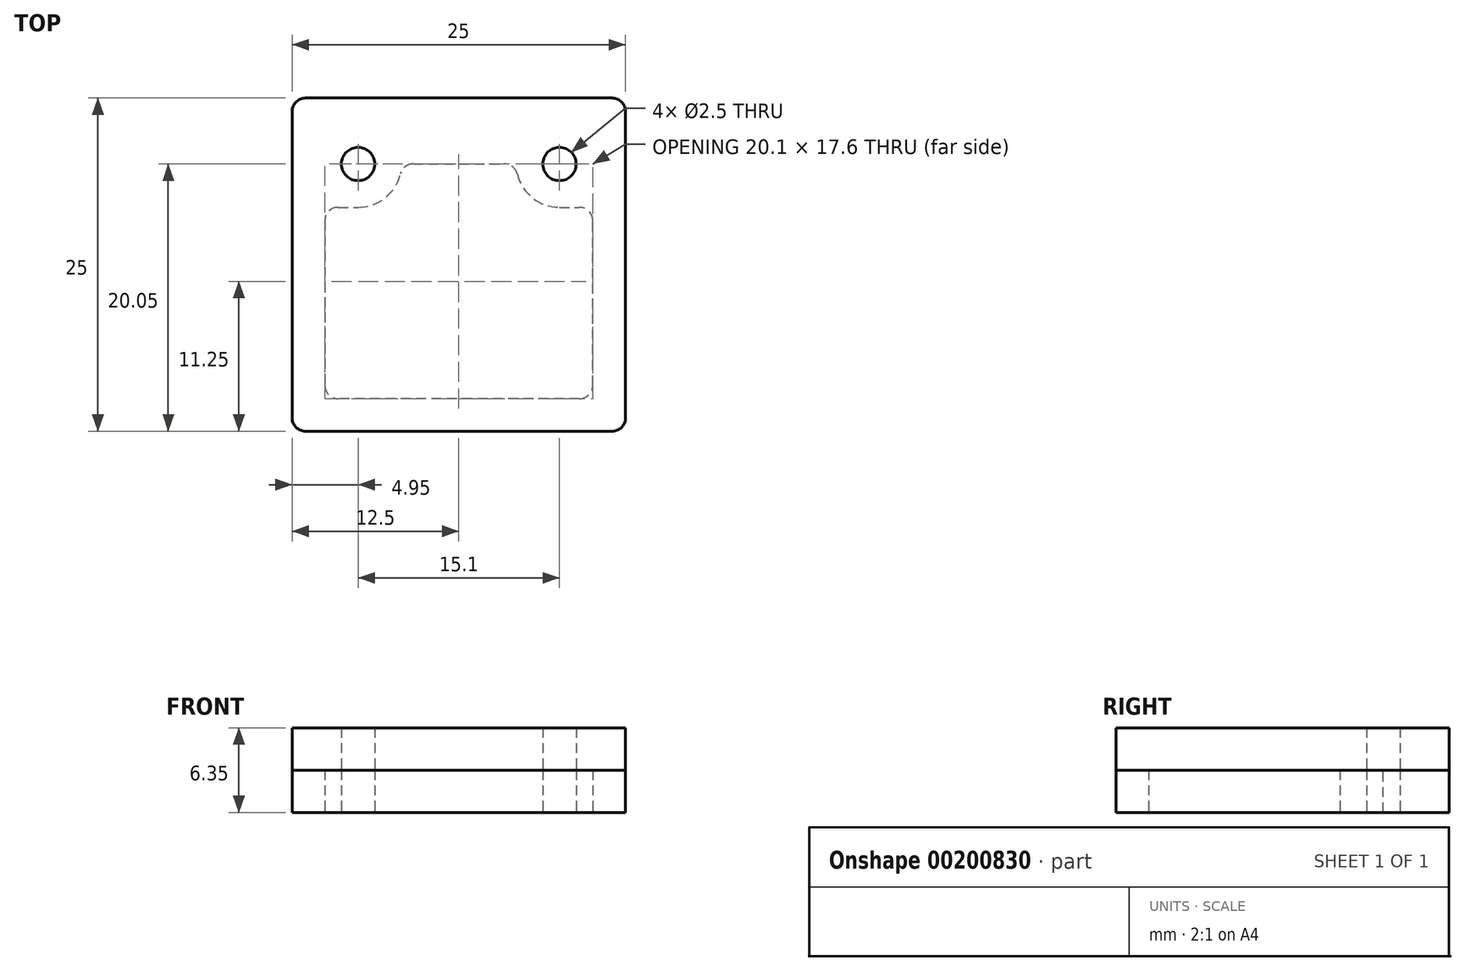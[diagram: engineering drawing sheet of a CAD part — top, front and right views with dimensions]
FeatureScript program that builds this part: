
annotation { "Feature Type Name" : "Feature", "Feature Type Description" : "" }
export const myFeature = defineFeature(function(context is Context, id is Id, definition is map)
    precondition{}
    {
        {
            var Q0;
            Q0=qCreatedBy(makeId("Top.planeOp"),FACE);
            var sketch = newSketch(context, id + "F0", { "sketchPlane" : qUnion([Q0])});
            skLineSegment(sketch, "E0.bottom", {"start": v(10.05, 10.05) * mm, "end": v(-10.05, 10.05) * mm});
            skLineSegment(sketch, "E0.top", {"start": v(10.05, -10.05) * mm, "end": v(-10.05, -10.05) * mm});
            skLineSegment(sketch, "E0.left", {"start": v(10.05, 10.05) * mm, "end": v(10.05, -10.05) * mm});
            skLineSegment(sketch, "E0.right", {"start": v(-10.05, 10.05) * mm, "end": v(-10.05, -10.05) * mm});
            skPoint(sketch, "E0.middle", {"position": v(0, 0) * mm});
            skCircle(sketch, "E1", {"center": v(-7.55, 7.55) * mm, "radius": 1.25 * mm});
            skLineSegment(sketch, "E2", {"start": v(0, 10.05) * mm, "end": v(0, -10.05) * mm, "construction": true});
            skCircle(sketch, "E3.MirrorC", {"center": v(7.55, 7.55) * mm, "radius": 1.25 * mm});
            skCircle(sketch, "E4.0", {"center": v(7.55, 7.55) * mm, "radius": 3.25 * mm});
            skCircle(sketch, "E5.0", {"center": v(-7.55, 7.55) * mm, "radius": 3.25 * mm});
            skLineSegment(sketch, "E6.bottom", {"start": v(12.5, 12.5) * mm, "end": v(-12.5, 12.5) * mm});
            skLineSegment(sketch, "E6.top", {"start": v(12.5, -12.5) * mm, "end": v(-12.5, -12.5) * mm});
            skLineSegment(sketch, "E6.left", {"start": v(12.5, 12.5) * mm, "end": v(12.5, -12.5) * mm});
            skLineSegment(sketch, "E6.right", {"start": v(-12.5, 12.5) * mm, "end": v(-12.5, -12.5) * mm});
            skSolve(sketch);
        }
        {
            var Q0;
            Q0=qCreatedBy(makeId("Top.planeOp"),FACE);
            var sketch = newSketch(context, id + "F1", { "sketchPlane" : qUnion([Q0])});
            skLineSegment(sketch, "E7.0", {"start": v(-12.5, 12.5) * mm, "end": v(-12.5, -12.5) * mm});
            skLineSegment(sketch, "E8.0", {"start": v(12.5, 12.5) * mm, "end": v(-12.5, 12.5) * mm});
            skLineSegment(sketch, "E9.0", {"start": v(12.5, 12.5) * mm, "end": v(12.5, -12.5) * mm});
            skLineSegment(sketch, "E10.0", {"start": v(12.5, -12.5) * mm, "end": v(-12.5, -12.5) * mm});
            skLineSegment(sketch, "E11.0", {"start": v(10.05, -10.05) * mm, "end": v(-10.05, -10.05) * mm});
            skArc(sketch, "E12.0", {"start": v(7.55, 4.3) * mm, "mid": v(5.25, 5.25) * mm, "end": v(4.3, 7.55) * mm});
            skArc(sketch, "E13.0.2", {"start": v(-4.3, 7.55) * mm, "mid": v(-5.25, 5.25) * mm, "end": v(-7.55, 4.3) * mm});
            skLineSegment(sketch, "E13.0.3", {"start": v(-10.05, 4.3) * mm, "end": v(-10.05, -10.05) * mm});
            skLineSegment(sketch, "E13.0.4", {"start": v(-10.05, -10.05) * mm, "end": v(10.05, -10.05) * mm});
            skLineSegment(sketch, "E13.0.5", {"start": v(10.05, -10.05) * mm, "end": v(10.05, 4.3) * mm});
            skLineSegment(sketch, "E14", {"start": v(-10.05, 4.3) * mm, "end": v(-7.55, 4.3) * mm});
            skLineSegment(sketch, "E15", {"start": v(7.55, 4.3) * mm, "end": v(10.05, 4.3) * mm});
            skLineSegment(sketch, "E16", {"start": v(-4.3, 7.55) * mm, "end": v(4.3, 7.55) * mm});
            skPoint(sketch, "E17.orphan", {"position": v(-5.47, 10.05) * mm});
            skPoint(sketch, "E18.orphan", {"position": v(5.47, 10.05) * mm});
            skPoint(sketch, "E19.orphan", {"position": v(10.05, 5.47) * mm});
            skPoint(sketch, "E20.orphan", {"position": v(-10.05, 5.47) * mm});
            skCircle(sketch, "E21.0", {"center": v(-7.55, 7.55) * mm, "radius": 1.25 * mm});
            skCircle(sketch, "E22.0", {"center": v(7.55, 7.55) * mm, "radius": 1.25 * mm});
            skSolve(sketch);
        }
        {
            var Q0;
            Q0 = qSketchRegion(id + "F1", true);
            extrude(context, id + "F2", {"entities" : qUnion([Q0]), "depth" : 3.17 * mm});
        }
        {
            var Q0;
            Q0=makeQuery(id+"F2.opExtrude","SWEPT_EDGE",EDGE,{"disambiguationData":[OSD([sQuery(id+"F1.wireOp",EDGE,"E7.0"),sQuery(id+"F1.wireOp",EDGE,"E8.0")])]});
            var Q1;
            Q1=makeQuery(id+"F2.opExtrude","SWEPT_EDGE",EDGE,{"disambiguationData":[OSD([sQuery(id+"F1.wireOp",EDGE,"E8.0"),sQuery(id+"F1.wireOp",EDGE,"E9.0")])]});
            var Q2;
            Q2=makeQuery(id+"F2.opExtrude","SWEPT_EDGE",EDGE,{"disambiguationData":[OSD([sQuery(id+"F1.wireOp",EDGE,"E9.0"),sQuery(id+"F1.wireOp",EDGE,"E10.0")])]});
            var Q3;
            Q3=makeQuery(id+"F2.opExtrude","SWEPT_EDGE",EDGE,{"disambiguationData":[OSD([sQuery(id+"F1.wireOp",EDGE,"E7.0"),sQuery(id+"F1.wireOp",EDGE,"E10.0")])]});
            var Q4;
            Q4=makeQuery(id+"F2.opExtrude","SWEPT_EDGE",EDGE,{"disambiguationData":[OSD([sQuery(id+"F1.wireOp",EDGE,"E13.0.3"),sQuery(id+"F1.wireOp",EDGE,"E13.0.4")])]});
            var Q5;
            Q5=makeQuery(id+"F2.opExtrude","SWEPT_EDGE",EDGE,{"disambiguationData":[OSD([sQuery(id+"F1.wireOp",EDGE,"E13.0.4"),sQuery(id+"F1.wireOp",EDGE,"E13.0.5")])]});
            var Q6;
            Q6=makeQuery(id+"F2.opExtrude","SWEPT_EDGE",EDGE,{"disambiguationData":[OSD([sQuery(id+"F1.wireOp",EDGE,"E13.0.3"),sQuery(id+"F1.wireOp",EDGE,"E14")])]});
            var Q7;
            Q7=makeQuery(id+"F2.opExtrude","SWEPT_EDGE",EDGE,{"disambiguationData":[OSD([sQuery(id+"F1.wireOp",EDGE,"E13.0.2"),sQuery(id+"F1.wireOp",EDGE,"E16")])]});
            var Q8;
            Q8=makeQuery(id+"F2.opExtrude","SWEPT_EDGE",EDGE,{"disambiguationData":[OSD([sQuery(id+"F1.wireOp",EDGE,"E12.0"),sQuery(id+"F1.wireOp",EDGE,"E16")])]});
            var Q9;
            Q9=makeQuery(id+"F2.opExtrude","SWEPT_EDGE",EDGE,{"disambiguationData":[OSD([sQuery(id+"F1.wireOp",EDGE,"E13.0.5"),sQuery(id+"F1.wireOp",EDGE,"E15")])]});
            fillet(context, id + "F3", {"entities" : qUnion([Q0, Q1, Q2, Q3, Q4, Q5, Q6, Q7, Q8, Q9]), "radius" : 1 * mm, "tangentPropagation" : true, "allowEdgeOverflow" : false});
        }
        {
            var Q0;
            Q0=makeQuery(id+"F2.opExtrude","CAP_FACE",FACE,{"disambiguationData":[OSD([sQuery(id+"F1.wireOp",EDGE,"E7.0"),sQuery(id+"F1.wireOp",EDGE,"E8.0"),sQuery(id+"F1.wireOp",EDGE,"E9.0"),sQuery(id+"F1.wireOp",EDGE,"E10.0"),sQuery(id+"F1.wireOp",EDGE,"E12.0"),sQuery(id+"F1.wireOp",EDGE,"E13.0.2"),sQuery(id+"F1.wireOp",EDGE,"E13.0.3"),sQuery(id+"F1.wireOp",EDGE,"E13.0.4"),sQuery(id+"F1.wireOp",EDGE,"E13.0.5"),sQuery(id+"F1.wireOp",EDGE,"E14"),sQuery(id+"F1.wireOp",EDGE,"E15"),sQuery(id+"F1.wireOp",EDGE,"E16"),sQuery(id+"F1.wireOp",EDGE,"E21.0"),sQuery(id+"F1.wireOp",EDGE,"E22.0")])],"isStart":false});
            var sketch = newSketch(context, id + "F4", { "sketchPlane" : qUnion([Q0])});
            skLineSegment(sketch, "E23.0", {"start": v(11.5, 12.5) * mm, "end": v(-11.5, 12.5) * mm});
            skArc(sketch, "E24.0", {"start": v(-11.5, 12.5) * mm, "mid": v(-12.2, 12.2) * mm, "end": v(-12.5, 11.5) * mm});
            skLineSegment(sketch, "E25.0", {"start": v(-12.5, 11.5) * mm, "end": v(-12.5, -11.5) * mm});
            skArc(sketch, "E26.0", {"start": v(-12.5, -11.5) * mm, "mid": v(-12.2, -12.2) * mm, "end": v(-11.5, -12.5) * mm});
            skLineSegment(sketch, "E27.0", {"start": v(11.5, -12.5) * mm, "end": v(-11.5, -12.5) * mm});
            skPoint(sketch, "E28.0", {"position": v(12.2, -12.2) * mm});
            skArc(sketch, "E29.0", {"start": v(11.5, -12.5) * mm, "mid": v(12.2, -12.2) * mm, "end": v(12.5, -11.5) * mm});
            skLineSegment(sketch, "E30.0", {"start": v(12.5, 11.5) * mm, "end": v(12.5, -11.5) * mm});
            skArc(sketch, "E31.0", {"start": v(12.5, 11.5) * mm, "mid": v(12.2, 12.2) * mm, "end": v(11.5, 12.5) * mm});
            skCircle(sketch, "E32.0", {"center": v(7.55, 7.55) * mm, "radius": 1.25 * mm});
            skCircle(sketch, "E33.0", {"center": v(-7.55, 7.55) * mm, "radius": 1.25 * mm});
            skSolve(sketch);
        }
        {
            var Q0;
            Q0 = qSketchRegion(id + "F4", true);
            extrude(context, id + "F5", {"entities" : qUnion([Q0]), "depth" : 3.17 * mm});
        }
    });
